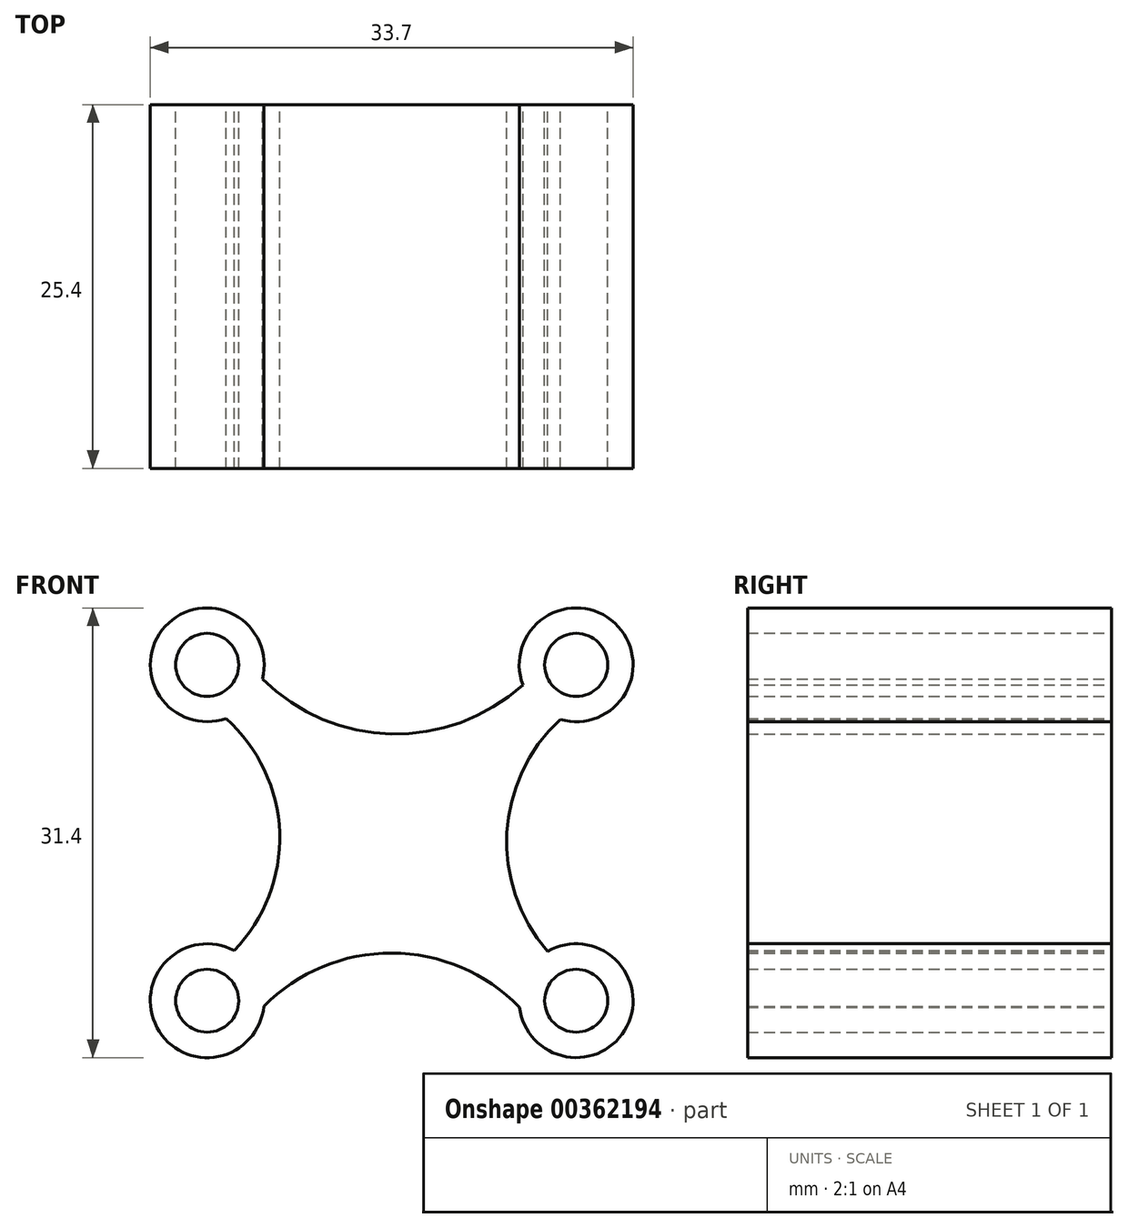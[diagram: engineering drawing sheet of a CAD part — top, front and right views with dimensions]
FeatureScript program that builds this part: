
annotation { "Feature Type Name" : "Feature", "Feature Type Description" : "" }
export const myFeature = defineFeature(function(context is Context, id is Id, definition is map)
    precondition{}
    {
        {
            var Q0;
            Q0=qCreatedBy(makeId("Front.planeOp"),FACE);
            var sketch = newSketch(context, id + "F0", { "sketchPlane" : qUnion([Q0])});
            skArc(sketch, "E0", {"start": v(-9.03, 10.75) * mm, "mid": v(-0.02, 6.9) * mm, "end": v(9.16, 10.33) * mm});
            skArc(sketch, "E1", {"start": v(11.84, 7.98) * mm, "mid": v(8.05, 0.04) * mm, "end": v(10.9, -8.29) * mm});
            skArc(sketch, "E2", {"start": v(8.93, -12.18) * mm, "mid": v(0.02, -8.4) * mm, "end": v(-8.92, -12.1) * mm});
            skArc(sketch, "E3", {"start": v(-11, -8.23) * mm, "mid": v(-7.82, 0) * mm, "end": v(-11.57, 7.98) * mm});
            skCircle(sketch, "E4", {"center": v(-12.88, 11.73) * mm, "radius": 3.97 * mm});
            skCircle(sketch, "E5.MirrorC", {"center": v(12.88, 11.73) * mm, "radius": 3.97 * mm});
            skCircle(sketch, "E6.MirrorC", {"center": v(-12.88, -11.73) * mm, "radius": 3.97 * mm});
            skCircle(sketch, "E7.MirrorC", {"center": v(12.88, -11.73) * mm, "radius": 3.97 * mm});
            skCircle(sketch, "E8", {"center": v(-12.88, 11.73) * mm, "radius": 2.2 * mm});
            skCircle(sketch, "E9.MirrorC", {"center": v(12.88, 11.73) * mm, "radius": 2.2 * mm});
            skCircle(sketch, "E10.MirrorC", {"center": v(-12.88, -11.73) * mm, "radius": 2.2 * mm});
            skCircle(sketch, "E11.MirrorC", {"center": v(12.88, -11.73) * mm, "radius": 2.2 * mm});
            skSolve(sketch);
        }
        {
            var Q0;
            Q0 = qSketchRegion(id + "F0", true);
            extrude(context, id + "F1", {"entities" : qUnion([Q0]), "depth" : 25.4 * mm});
        }
    });
